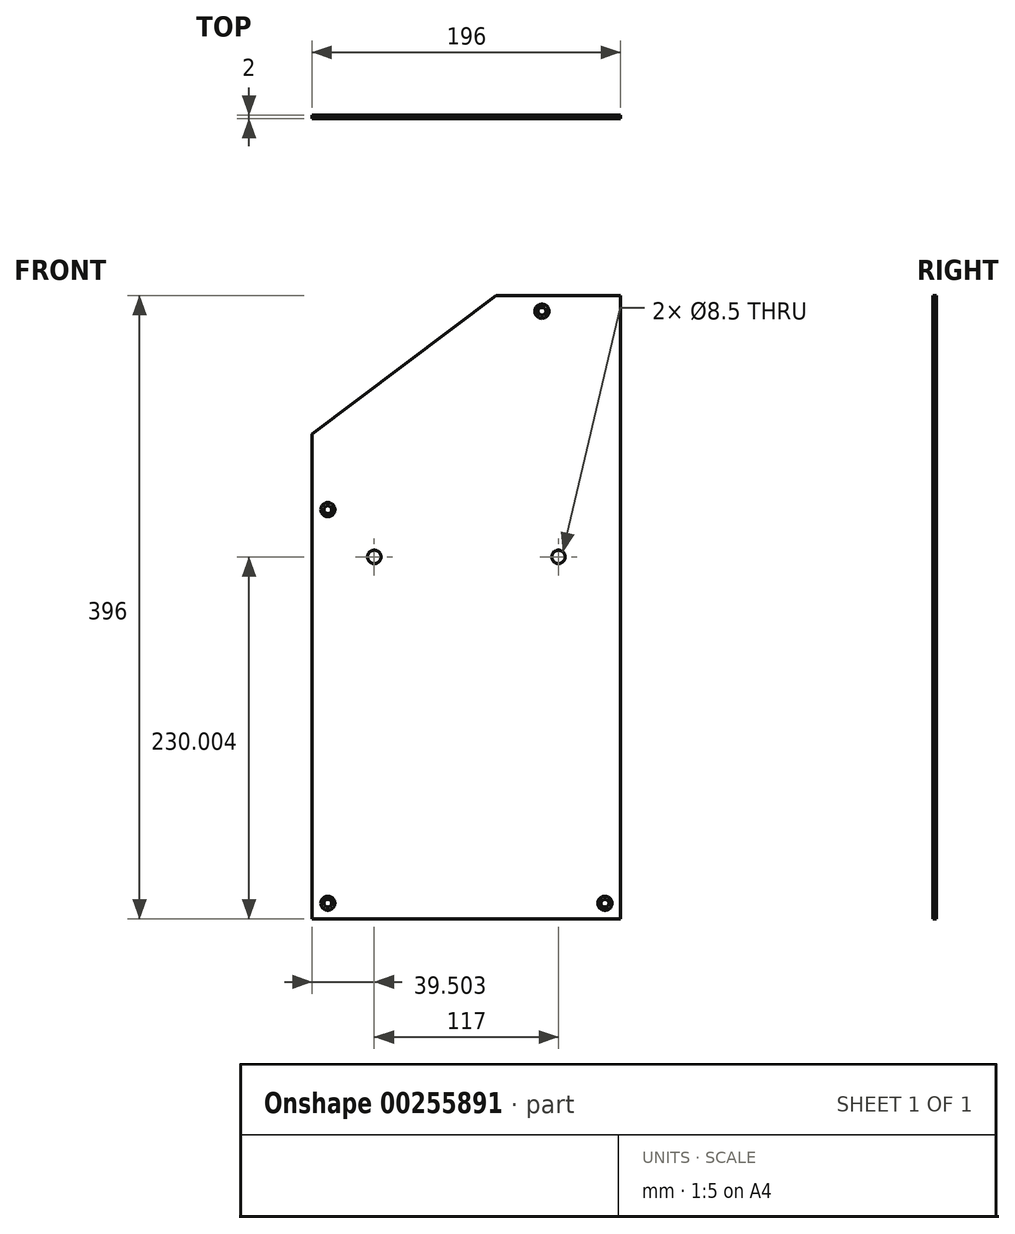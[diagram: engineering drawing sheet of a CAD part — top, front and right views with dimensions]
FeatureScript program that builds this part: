
annotation { "Feature Type Name" : "Feature", "Feature Type Description" : "" }
export const myFeature = defineFeature(function(context is Context, id is Id, definition is map)
    precondition{}
    {
        {
            var Q0;
            Q0=qCreatedBy(makeId("Front.planeOp"),FACE);
            var sketch = newSketch(context, id + "F0", { "sketchPlane" : qUnion([Q0])});
            skLineSegment(sketch, "E0", {"start": v(-180.77, -183.47) * mm, "end": v(-180.77, 124.53) * mm});
            skLineSegment(sketch, "E1", {"start": v(-180.77, 124.53) * mm, "end": v(-63.99, 212.53) * mm});
            skLineSegment(sketch, "E2", {"start": v(-63.99, 212.53) * mm, "end": v(15.23, 212.53) * mm});
            skLineSegment(sketch, "E3", {"start": v(15.23, 212.53) * mm, "end": v(15.23, -183.47) * mm});
            skLineSegment(sketch, "E4", {"start": v(15.23, -183.47) * mm, "end": v(-180.77, -183.47) * mm});
            skLineSegment(sketch, "E5", {"start": v(-180.77, 124.53) * mm, "end": v(15.23, 124.53) * mm, "construction": true});
            skPoint(sketch, "E6", {"position": v(-141.27, 46.53) * mm});
            skPoint(sketch, "E7", {"position": v(-24.27, 46.53) * mm});
            skPoint(sketch, "E8", {"position": v(5.23, 202.53) * mm});
            skPoint(sketch, "E9", {"position": v(-34.77, 202.53) * mm});
            skPoint(sketch, "E10", {"position": v(-170.77, -173.47) * mm});
            skPoint(sketch, "E11", {"position": v(5.23, -173.47) * mm});
            skPoint(sketch, "E12", {"position": v(-170.77, 76.53) * mm});
            skLineSegment(sketch, "E13", {"start": v(-141.27, 46.53) * mm, "end": v(-24.27, 46.53) * mm, "construction": true});
            skPoint(sketch, "E14", {"position": v(-82.77, 46.53) * mm});
            skLineSegment(sketch, "E15", {"start": v(-141.27, 46.53) * mm, "end": v(-180.77, 46.53) * mm, "construction": true});
            skLineSegment(sketch, "E16", {"start": v(-24.27, 46.53) * mm, "end": v(15.23, 46.53) * mm, "construction": true});
            skPoint(sketch, "E17", {"position": v(5.23, 76.53) * mm});
            skSolve(sketch);
        }
        {
            var Q0;
            Q0=makeQuery(id+"F0.imprint","IMPRINT",FACE,{"disambiguationData":[TD([[makeQuery(id+"F0.imprint","IMPRINT",EDGE,{"derivedFrom":sQuery(id+"F0.wireOp",EDGE,"E0")}),-1.0]])]});
            extrude(context, id + "F1", {"entities" : qUnion([Q0]), "oppositeDirection" : true, "depth" : 2 * mm});
        }
        {
            var Q0;
            Q0=sQuery(id+"F0.wireOp",VERTEX,"E6");
            var Q1;
            Q1=sQuery(id+"F0.wireOp",VERTEX,"E7");
            var Q2;
            Q2=makeQuery(id+"F1.opExtrude","SWEPT_BODY",BODY,{"disambiguationData":[OSD([sQuery(id+"F0.wireOp",EDGE,"E0"),sQuery(id+"F0.wireOp",EDGE,"E1"),sQuery(id+"F0.wireOp",EDGE,"E2"),sQuery(id+"F0.wireOp",EDGE,"E3"),sQuery(id+"F0.wireOp",EDGE,"E4")])]});
            hole(context, id + "F2", {"style" : HoleStyle.SIMPLE, "endStyle" : HoleEndStyle.BLIND, "holeDiameter" : 8.5 * mm, "holeDepth" : 15.75 * mm, "tappedDepth" : 12 * mm, "tapClearance" : 3, "startFromSketch" : true, "locations" : qUnion([Q0, Q1]), "scope" : qUnion([Q2])});
        }
        {
            var Q0;
            Q0=sQuery(id+"F0.wireOp",VERTEX,"E12");
            var Q1;
            Q1=sQuery(id+"F0.wireOp",VERTEX,"E9");
            var Q2;
            Q2=sQuery(id+"F0.wireOp",VERTEX,"E11");
            var Q3;
            Q3=sQuery(id+"F0.wireOp",VERTEX,"E10");
            var Q4;
            Q4=makeQuery(id+"F1.opExtrude","SWEPT_BODY",BODY,{"disambiguationData":[OSD([sQuery(id+"F0.wireOp",EDGE,"E0"),sQuery(id+"F0.wireOp",EDGE,"E1"),sQuery(id+"F0.wireOp",EDGE,"E2"),sQuery(id+"F0.wireOp",EDGE,"E3"),sQuery(id+"F0.wireOp",EDGE,"E4")])]});
            hole(context, id + "F3", {"style" : HoleStyle.C_SINK, "endStyle" : HoleEndStyle.THROUGH, "standardTappedOrClearance" : lookupTablePath({ "standard" : "ISO", "fit" : "Normal", "size" : "M4", "type" : "Clearance" }), "standardBlindInLast" : lookupTablePath({ "fit" : "Standard", "standard" : "ISO", "size" : "M4", "type" : "Clearance" }), "holeDiameter" : 4.4 * mm, "cSinkDiameter" : 8.96 * mm, "cSinkAngle" : 90 * degree, "tappedDepth" : 12 * mm, "tapClearance" : 3, "startFromSketch" : true, "locations" : qUnion([Q0, Q1, Q2, Q3]), "scope" : qUnion([Q4])});
        }
    });
